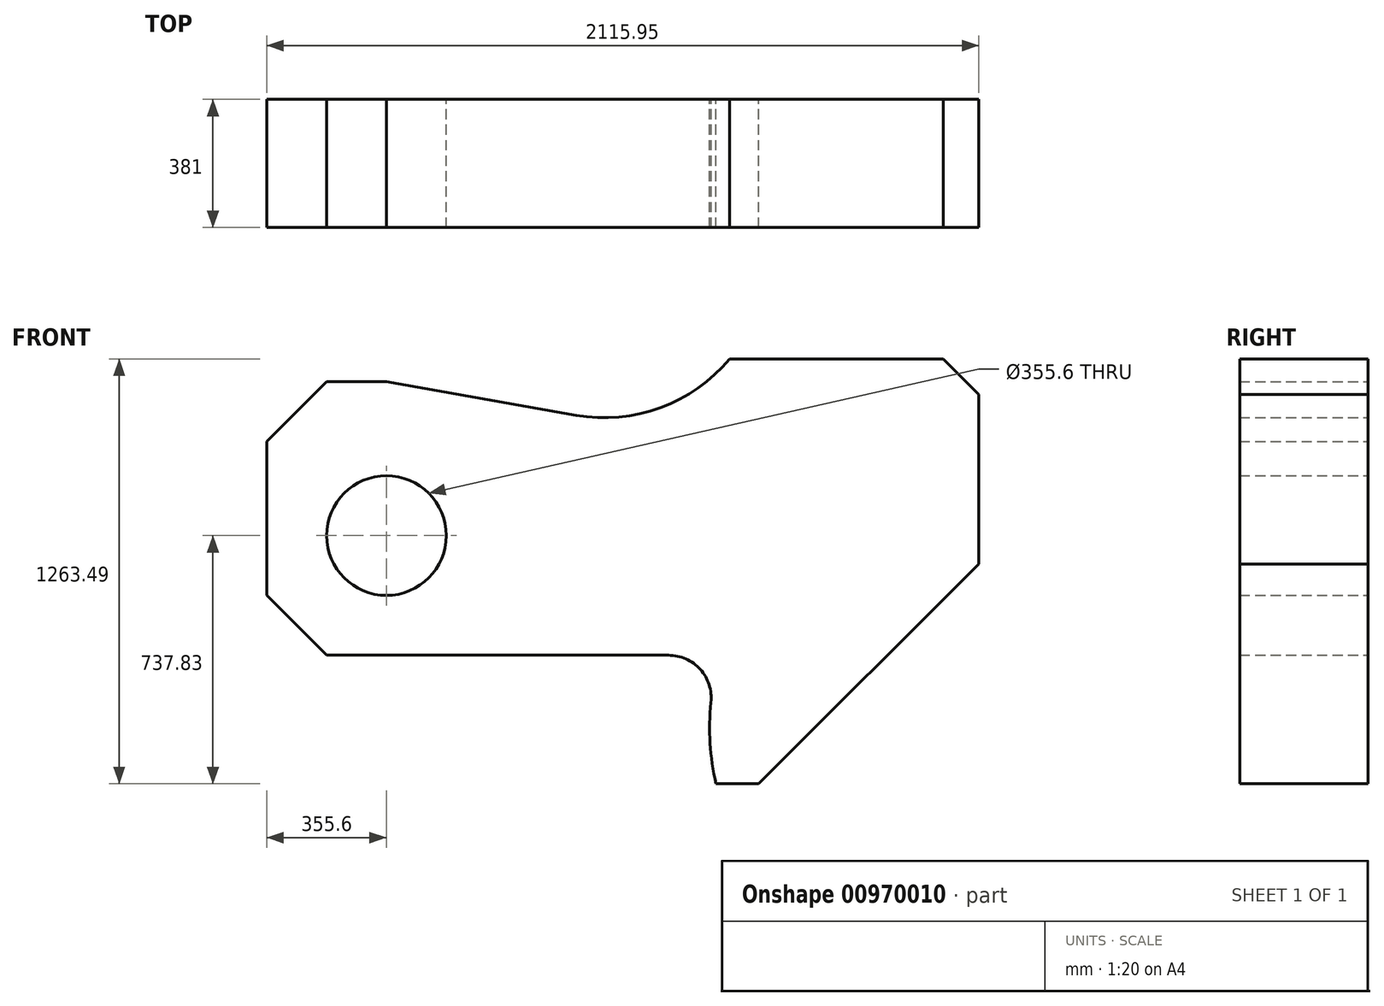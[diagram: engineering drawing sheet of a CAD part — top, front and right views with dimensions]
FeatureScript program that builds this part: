
annotation { "Feature Type Name" : "Feature", "Feature Type Description" : "" }
export const myFeature = defineFeature(function(context is Context, id is Id, definition is map)
    precondition{}
    {
        {
            var Q0;
            Q0=qCreatedBy(makeId("Front.planeOp"),FACE);
            var sketch = newSketch(context, id + "F0", { "sketchPlane" : qUnion([Q0])});
            skCircle(sketch, "E0", {"center": v(0, 0) * mm, "radius": 177.8 * mm});
            skLineSegment(sketch, "E1", {"start": v(-355.6, 0) * mm, "end": v(-355.6, -177.8) * mm});
            skLineSegment(sketch, "E2", {"start": v(-355.6, -177.8) * mm, "end": v(-177.8, -355.6) * mm});
            skLineSegment(sketch, "E3", {"start": v(0, -355.6) * mm, "end": v(-177.8, -355.6) * mm});
            skLineSegment(sketch, "E4", {"start": v(0, -355.6) * mm, "end": v(838.2, -355.6) * mm});
            skLineSegment(sketch, "E5", {"start": v(-355.6, 0) * mm, "end": v(-355.6, 279.4) * mm});
            skLineSegment(sketch, "E6", {"start": v(-355.6, 279.4) * mm, "end": v(-177.8, 457.2) * mm});
            skLineSegment(sketch, "E7", {"start": v(-177.8, 457.2) * mm, "end": v(0, 457.2) * mm});
            skLineSegment(sketch, "E8", {"start": v(0, 457.2) * mm, "end": v(564.05, 357.74) * mm});
            skLineSegment(sketch, "E9", {"start": v(0, 457.2) * mm, "end": v(267.82, 457.2) * mm, "construction": true});
            skArc(sketch, "E10", {"start": v(563.53, 357.83) * mm, "mid": v(814.08, 380.23) * mm, "end": v(1019.33, 525.66) * mm});
            skLineSegment(sketch, "E11", {"start": v(0, 0) * mm, "end": v(0, 525.66) * mm, "construction": true});
            skLineSegment(sketch, "E12", {"start": v(1019.33, 525.66) * mm, "end": v(1654.33, 525.66) * mm});
            skLineSegment(sketch, "E13", {"start": v(1106.46, -737.83) * mm, "end": v(1760.35, -83.94) * mm});
            skLineSegment(sketch, "E14", {"start": v(1106.46, -737.83) * mm, "end": v(979.46, -737.83) * mm});
            skLineSegment(sketch, "E15.0", {"start": v(1590.22, -255.23) * mm, "end": v(1589.06, -255.23) * mm});
            skArc(sketch, "E16", {"start": v(964.52, -495.75) * mm, "mid": v(932.54, -397.57) * mm, "end": v(838.2, -355.6) * mm});
            skArc(sketch, "E17.trimOffspring", {"start": v(964.52, -495.75) * mm, "mid": v(961.96, -617.4) * mm, "end": v(979.46, -737.83) * mm});
            skLineSegment(sketch, "E18", {"start": v(1760.35, 419.65) * mm, "end": v(1760.35, -83.94) * mm});
            skLineSegment(sketch, "E19", {"start": v(1654.33, 525.66) * mm, "end": v(1760.35, 419.65) * mm});
            skLineSegment(sketch, "E20", {"start": v(1654.33, 525.66) * mm, "end": v(1788.48, 525.66) * mm, "construction": true});
            skSolve(sketch);
        }
        {
            var Q0;
            Q0=makeQuery(id+"F0.imprint","IMPRINT",FACE,{"disambiguationData":[TD([[makeQuery(id+"F0.imprint","IMPRINT",EDGE,{"derivedFrom":sQuery(id+"F0.wireOp",EDGE,"E0")}),-1.0]])]});
            extrude(context, id + "F1", {"entities" : qUnion([Q0]), "depth" : 381 * mm, "offsetDistance" : 25.4 * mm});
        }
    });
